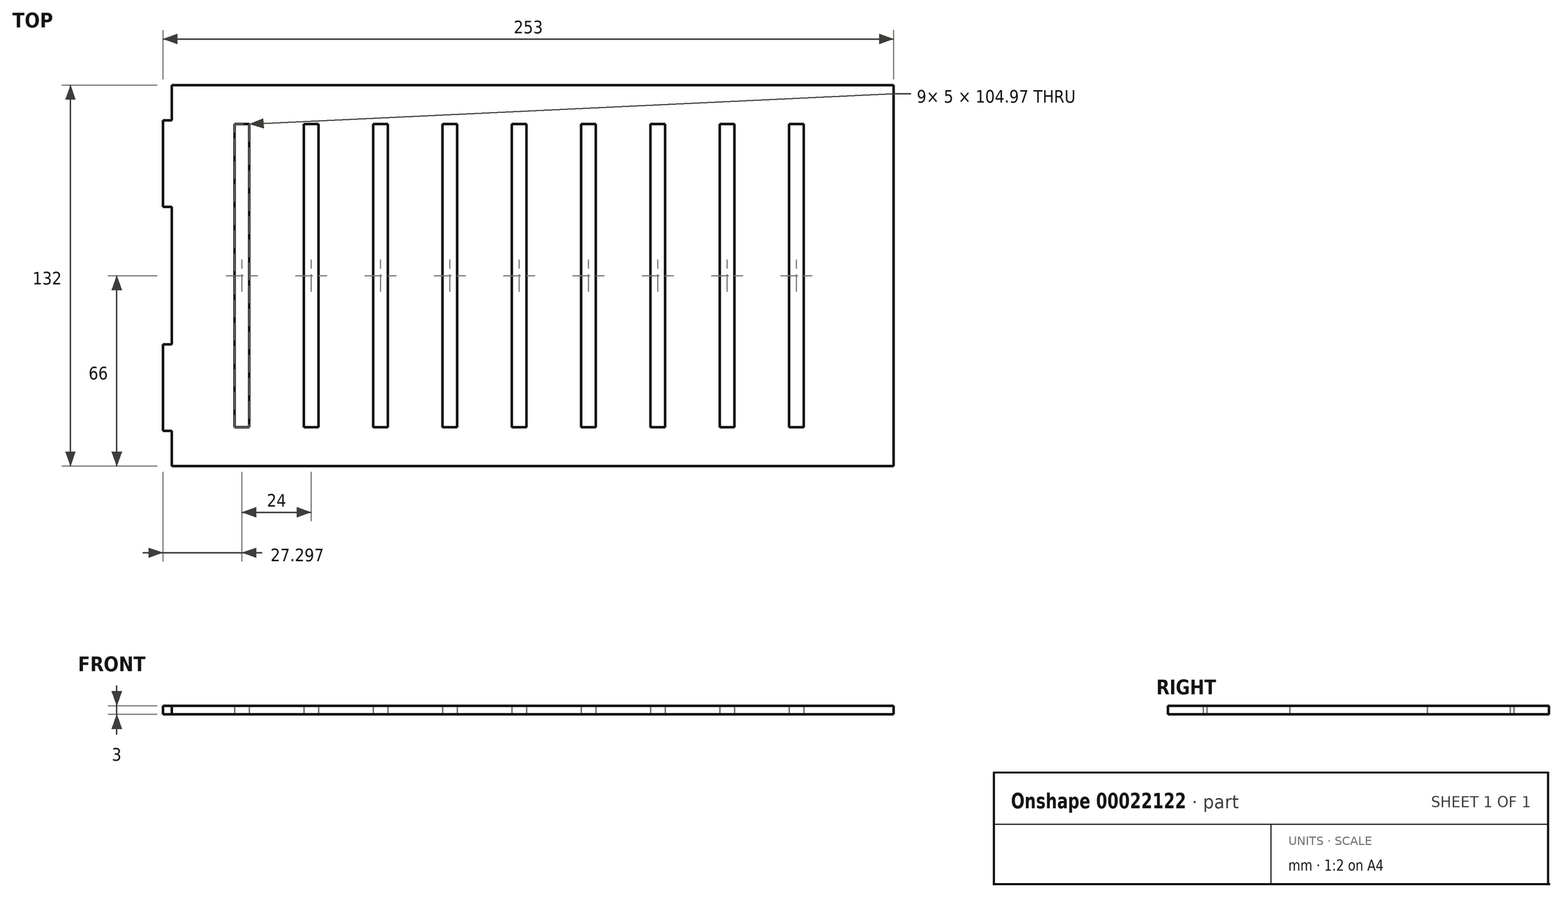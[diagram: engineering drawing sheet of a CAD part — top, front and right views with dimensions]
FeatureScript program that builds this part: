
annotation { "Feature Type Name" : "Feature", "Feature Type Description" : "" }
export const myFeature = defineFeature(function(context is Context, id is Id, definition is map)
    precondition{}
    {
        {
            var Q0;
            Q0=qCreatedBy(makeId("Top.planeOp"),FACE);
            var sketch = newSketch(context, id + "F0", { "sketchPlane" : qUnion([Q0])});
            skLineSegment(sketch, "E0.rect.bottom", {"start": v(110.27, -108) * mm, "end": v(-139.73, -108) * mm});
            skLineSegment(sketch, "E0.rect.top", {"start": v(110.27, 24) * mm, "end": v(-139.73, 24) * mm});
            skLineSegment(sketch, "E0.rect.left", {"start": v(110.27, -108) * mm, "end": v(110.27, 24) * mm});
            skLineSegment(sketch, "E1", {"start": v(110.27, -42) * mm, "end": v(-149.14, -42) * mm, "construction": true});
            skLineSegment(sketch, "E2", {"start": v(-139.73, -42) * mm, "end": v(-139.73, -65.78) * mm});
            skLineSegment(sketch, "E3", {"start": v(-139.73, -65.78) * mm, "end": v(-142.73, -65.78) * mm});
            skLineSegment(sketch, "E4", {"start": v(-142.73, -65.78) * mm, "end": v(-142.73, -95.78) * mm});
            skLineSegment(sketch, "E5", {"start": v(-142.73, -95.78) * mm, "end": v(-139.73, -95.78) * mm});
            skLineSegment(sketch, "E6", {"start": v(-139.73, -95.78) * mm, "end": v(-139.73, -108) * mm});
            skLineSegment(sketch, "E7.MirrorCS", {"start": v(-139.73, -42) * mm, "end": v(-139.73, -18.22) * mm});
            skLineSegment(sketch, "E8.MirrorCS", {"start": v(-142.73, -18.22) * mm, "end": v(-142.73, 11.78) * mm});
            skLineSegment(sketch, "E9.MirrorCS", {"start": v(-139.73, 11.78) * mm, "end": v(-139.73, 24) * mm});
            skLineSegment(sketch, "E10.MirrorCS", {"start": v(-142.73, 11.78) * mm, "end": v(-139.73, 11.78) * mm});
            skLineSegment(sketch, "E11.MirrorCS", {"start": v(-139.73, -18.22) * mm, "end": v(-142.73, -18.22) * mm});
            skLineSegment(sketch, "E12.rect.bottom", {"start": v(-16.93, -94.49) * mm, "end": v(-21.93, -94.49) * mm});
            skLineSegment(sketch, "E12.rect.top", {"start": v(-16.93, 10.49) * mm, "end": v(-21.93, 10.49) * mm});
            skLineSegment(sketch, "E12.rect.left", {"start": v(-16.93, -94.49) * mm, "end": v(-16.93, 10.49) * mm});
            skLineSegment(sketch, "E12.rect.right", {"start": v(-21.93, -94.49) * mm, "end": v(-21.93, 10.49) * mm});
            skPoint(sketch, "E12.rect.middle", {"position": v(-19.43, -42) * mm});
            skLineSegment(sketch, "E13.1.0.0", {"start": v(-40.93, -94.49) * mm, "end": v(-40.93, 10.49) * mm});
            skPoint(sketch, "E13.1.0.3", {"position": v(-43.43, -42) * mm});
            skLineSegment(sketch, "E13.1.0.4", {"start": v(-45.93, -94.49) * mm, "end": v(-45.93, 10.49) * mm});
            skLineSegment(sketch, "E13.1.0.11", {"start": v(-40.93, 10.49) * mm, "end": v(-45.93, 10.49) * mm});
            skLineSegment(sketch, "E13.1.0.12", {"start": v(-40.93, -94.49) * mm, "end": v(-45.93, -94.49) * mm});
            skLineSegment(sketch, "E13.2.0.0", {"start": v(-64.93, -94.49) * mm, "end": v(-64.93, 10.49) * mm});
            skPoint(sketch, "E13.2.0.3", {"position": v(-67.43, -42) * mm});
            skLineSegment(sketch, "E13.2.0.4", {"start": v(-69.93, -94.49) * mm, "end": v(-69.93, 10.49) * mm});
            skLineSegment(sketch, "E13.2.0.11", {"start": v(-64.93, 10.49) * mm, "end": v(-69.93, 10.49) * mm});
            skLineSegment(sketch, "E13.2.0.12", {"start": v(-64.93, -94.49) * mm, "end": v(-69.93, -94.49) * mm});
            skLineSegment(sketch, "E13.3.0.0", {"start": v(-88.93, -94.49) * mm, "end": v(-88.93, 10.49) * mm});
            skPoint(sketch, "E13.3.0.3", {"position": v(-91.43, -42) * mm});
            skLineSegment(sketch, "E13.3.0.4", {"start": v(-93.93, -94.49) * mm, "end": v(-93.93, 10.49) * mm});
            skLineSegment(sketch, "E13.3.0.11", {"start": v(-88.93, 10.49) * mm, "end": v(-93.93, 10.49) * mm});
            skLineSegment(sketch, "E13.3.0.12", {"start": v(-88.93, -94.49) * mm, "end": v(-93.93, -94.49) * mm});
            skLineSegment(sketch, "E13.4.0.0", {"start": v(-112.93, -94.49) * mm, "end": v(-112.93, 10.49) * mm});
            skPoint(sketch, "E13.4.0.3", {"position": v(-115.43, -42) * mm});
            skLineSegment(sketch, "E13.4.0.4", {"start": v(-117.93, -94.49) * mm, "end": v(-117.93, 10.49) * mm});
            skLineSegment(sketch, "E13.4.0.11", {"start": v(-112.93, 10.49) * mm, "end": v(-117.93, 10.49) * mm});
            skLineSegment(sketch, "E13.4.0.12", {"start": v(-112.93, -94.49) * mm, "end": v(-117.93, -94.49) * mm});
            skLineSegment(sketch, "E14.1.0.2", {"start": v(2.07, -94.49) * mm, "end": v(2.07, 10.49) * mm});
            skPoint(sketch, "E14.1.0.4", {"position": v(4.57, -42) * mm});
            skLineSegment(sketch, "E14.1.0.6", {"start": v(7.07, -94.49) * mm, "end": v(7.07, 10.49) * mm});
            skLineSegment(sketch, "E14.1.0.7", {"start": v(7.07, 10.49) * mm, "end": v(2.07, 10.49) * mm});
            skLineSegment(sketch, "E14.1.0.8", {"start": v(7.07, -94.49) * mm, "end": v(2.07, -94.49) * mm});
            skLineSegment(sketch, "E14.2.0.2", {"start": v(26.07, -94.49) * mm, "end": v(26.07, 10.49) * mm});
            skPoint(sketch, "E14.2.0.4", {"position": v(28.57, -42) * mm});
            skLineSegment(sketch, "E14.2.0.6", {"start": v(31.07, -94.49) * mm, "end": v(31.07, 10.49) * mm});
            skLineSegment(sketch, "E14.2.0.7", {"start": v(31.07, 10.49) * mm, "end": v(26.07, 10.49) * mm});
            skLineSegment(sketch, "E14.2.0.8", {"start": v(31.07, -94.49) * mm, "end": v(26.07, -94.49) * mm});
            skLineSegment(sketch, "E14.3.0.2", {"start": v(50.07, -94.49) * mm, "end": v(50.07, 10.49) * mm});
            skPoint(sketch, "E14.3.0.4", {"position": v(52.57, -42) * mm});
            skLineSegment(sketch, "E14.3.0.6", {"start": v(55.07, -94.49) * mm, "end": v(55.07, 10.49) * mm});
            skLineSegment(sketch, "E14.3.0.7", {"start": v(55.07, 10.49) * mm, "end": v(50.07, 10.49) * mm});
            skLineSegment(sketch, "E14.3.0.8", {"start": v(55.07, -94.49) * mm, "end": v(50.07, -94.49) * mm});
            skLineSegment(sketch, "E14.4.0.2", {"start": v(74.07, -94.49) * mm, "end": v(74.07, 10.49) * mm});
            skPoint(sketch, "E14.4.0.4", {"position": v(76.57, -42) * mm});
            skLineSegment(sketch, "E14.4.0.6", {"start": v(79.07, -94.49) * mm, "end": v(79.07, 10.49) * mm});
            skLineSegment(sketch, "E14.4.0.7", {"start": v(79.07, 10.49) * mm, "end": v(74.07, 10.49) * mm});
            skLineSegment(sketch, "E14.4.0.8", {"start": v(79.07, -94.49) * mm, "end": v(74.07, -94.49) * mm});
            skSolve(sketch);
        }
        {
            var Q0;
            Q0=qSketchRegion(id+"F0",true);
            extrude(context, id + "F1", {"entities" : qUnion([Q0]), "depth" : 3 * mm});
        }
    });
